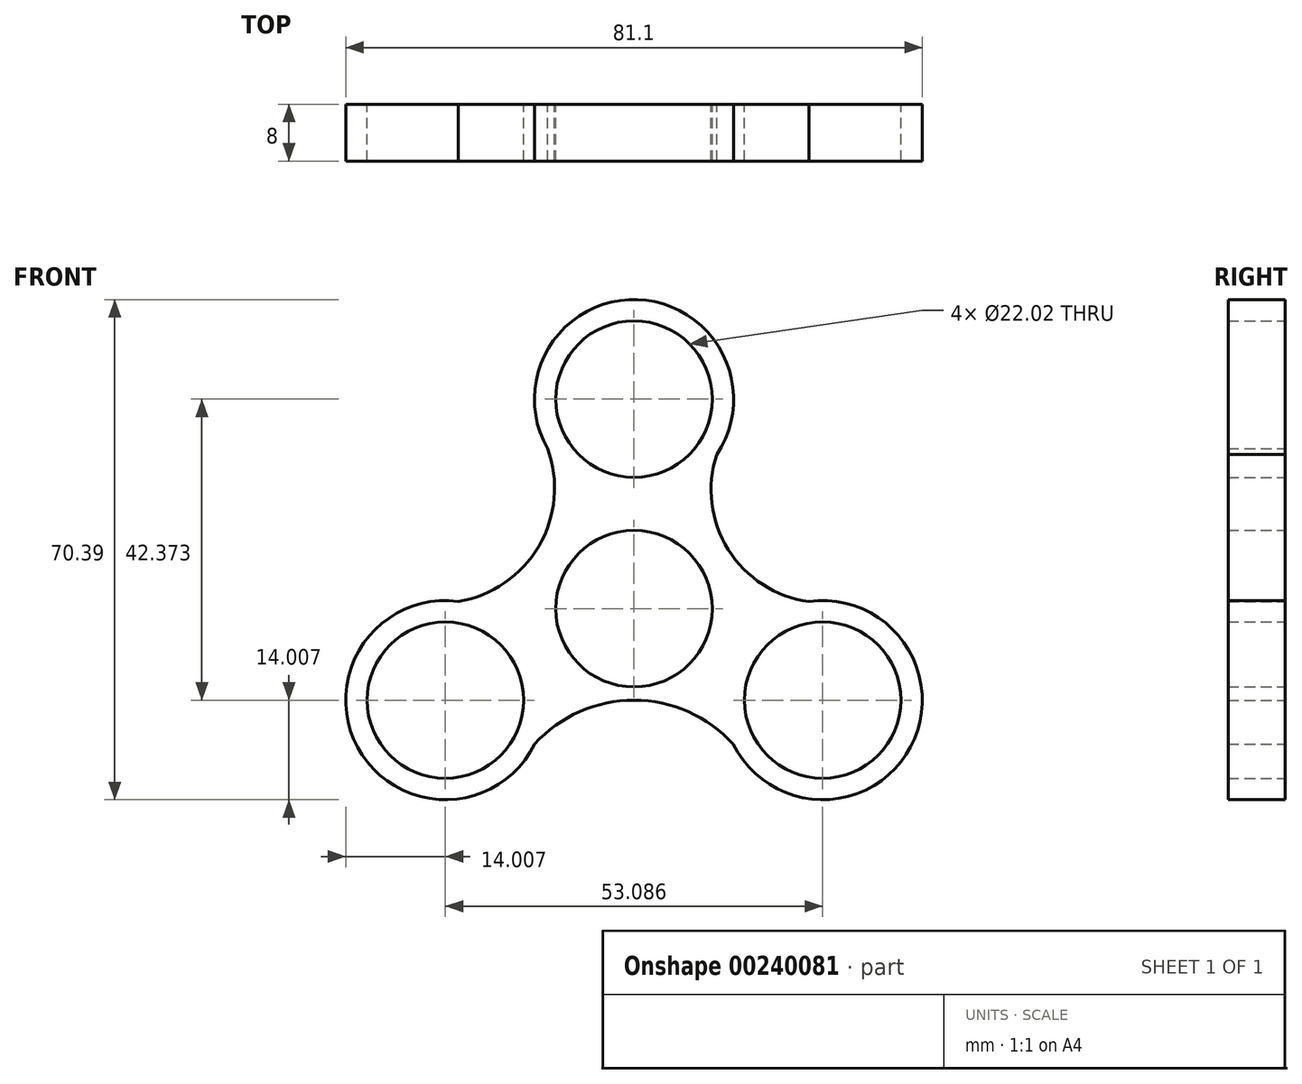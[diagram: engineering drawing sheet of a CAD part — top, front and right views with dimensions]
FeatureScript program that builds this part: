
annotation { "Feature Type Name" : "Feature", "Feature Type Description" : "" }
export const myFeature = defineFeature(function(context is Context, id is Id, definition is map)
    precondition{}
    {
        {
            var Q0;
            Q0=qCreatedBy(makeId("Front.planeOp"),FACE);
            var sketch = newSketch(context, id + "F0", { "sketchPlane" : qUnion([Q0])});
            skCircle(sketch, "E0", {"center": v(0, 0) * mm, "radius": 11.01 * mm});
            skCircle(sketch, "E1", {"center": v(0, 29.5) * mm, "radius": 11.01 * mm});
            skCircle(sketch, "E2", {"center": v(26.54, -12.87) * mm, "radius": 11.01 * mm});
            skCircle(sketch, "E3", {"center": v(-26.54, -12.87) * mm, "radius": 11.01 * mm});
            skLineSegment(sketch, "E4", {"start": v(0, -12.87) * mm, "end": v(0, -12.87) * mm});
            skLineSegment(sketch, "E5", {"start": v(13.27, 8.31) * mm, "end": v(13.27, 8.31) * mm});
            skArc(sketch, "E6", {"start": v(13.97, -19.05) * mm, "mid": v(38.92, -19.43) * mm, "end": v(24.6, 1) * mm});
            skArc(sketch, "E7", {"start": v(-24.73, 1.02) * mm, "mid": v(-38.89, -19.5) * mm, "end": v(-13.96, -19.04) * mm});
            skArc(sketch, "E8", {"start": v(11.64, 21.7) * mm, "mid": v(0.5, 43.5) * mm, "end": v(-12.16, 22.53) * mm});
            skArc(sketch, "E9", {"start": v(11.64, 21.7) * mm, "mid": v(13.27, 8.32) * mm, "end": v(24.6, 1) * mm});
            skPoint(sketch, "E9.first.point", {"position": v(11.64, 21.7) * mm});
            skPoint(sketch, "E9.third.point", {"position": v(24.6, 1) * mm});
            skArc(sketch, "E10", {"start": v(-24.73, 1.02) * mm, "mid": v(-13.38, 8.82) * mm, "end": v(-12.16, 22.53) * mm});
            skPoint(sketch, "E10.first.point", {"position": v(-12.16, 22.53) * mm});
            skPoint(sketch, "E10.second.point", {"position": v(-24.73, 1.02) * mm});
            skArc(sketch, "E11", {"start": v(13.97, -19.05) * mm, "mid": v(0, -12.87) * mm, "end": v(-13.96, -19.04) * mm});
            skPoint(sketch, "E11.first.point", {"position": v(-13.96, -19.04) * mm});
            skPoint(sketch, "E11.third.point", {"position": v(13.97, -19.05) * mm});
            skSolve(sketch);
        }
        {
            var Q0;
            Q0 = qSketchRegion(id + "F0", true);
            extrude(context, id + "F1", {"entities" : qUnion([Q0]), "depth" : 8 * mm, "offsetDistance" : 25 * mm});
        }
    });
